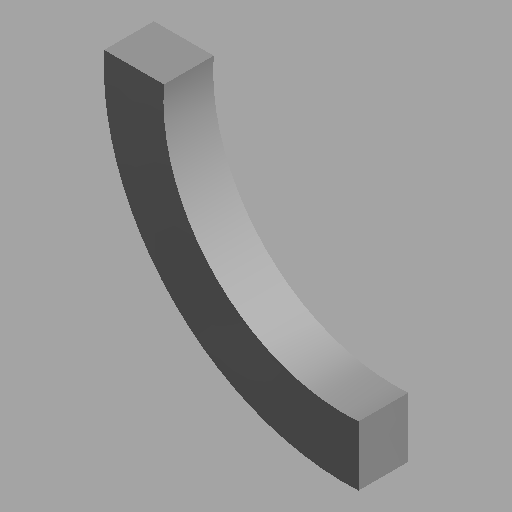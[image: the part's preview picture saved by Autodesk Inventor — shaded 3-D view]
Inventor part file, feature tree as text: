
AUTODESK INVENTOR PART (.ipt)
format: ipt  version: 2023 (Build 270158030, 158C)  size: 92,160 bytes
history: native  units: mm (DEFAULTED — no unit token found)
features: other x1, direct_edit x1, revolve x1
ambient origin geometry x8: Origin, YZ Plane, XZ Plane, XY Plane, X Axis, Y Axis, Z Axis, Center Point
bodies: Solid1 (feature_tree)
feature tree (3):
  other  "Arch header 1 (C)"
  direct_edit  "Direct Edit1"
  revolve  "Rotate1"  Angle=45.0deg
